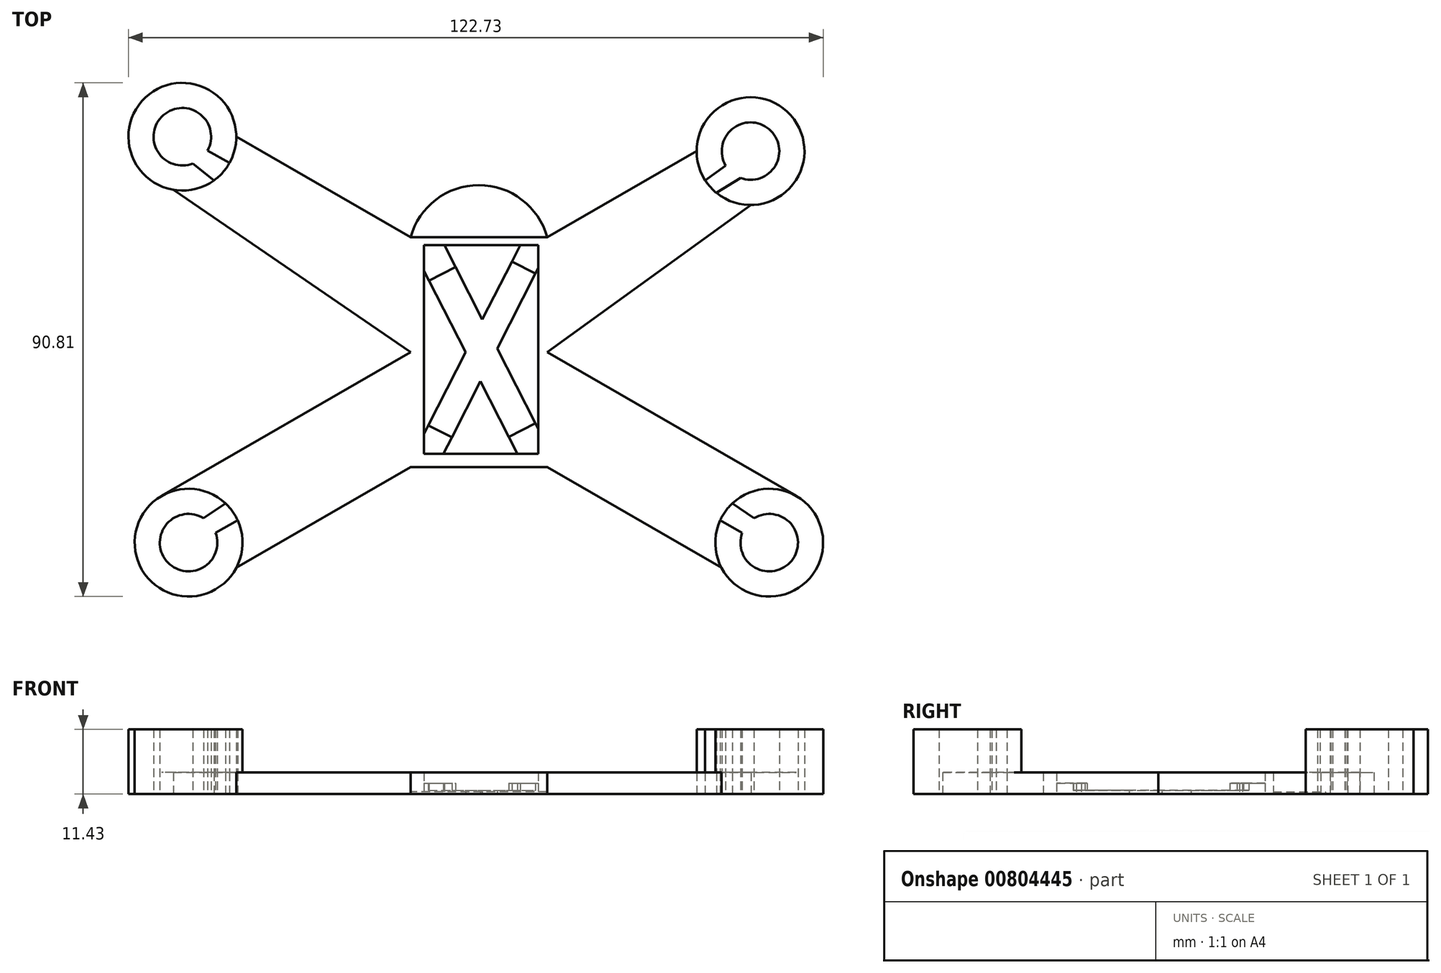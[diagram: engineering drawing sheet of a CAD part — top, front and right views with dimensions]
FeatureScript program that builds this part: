
annotation { "Feature Type Name" : "Feature", "Feature Type Description" : "" }
export const myFeature = defineFeature(function(context is Context, id is Id, definition is map)
    precondition{}
    {
        {
            var Q0;
            Q0=qCreatedBy(makeId("Top.planeOp"),FACE);
            var sketch = newSketch(context, id + "F0", { "sketchPlane" : qUnion([Q0])});
            skLineSegment(sketch, "E0.bottom", {"start": v(0, 0) * mm, "end": v(-24.13, 0) * mm});
            skLineSegment(sketch, "E0.top", {"start": v(0, 40.64) * mm, "end": v(-24.13, 40.64) * mm});
            skLineSegment(sketch, "E0.left", {"start": v(0, 0) * mm, "end": v(0, 40.64) * mm});
            skLineSegment(sketch, "E0.right", {"start": v(-24.13, 0) * mm, "end": v(-24.13, 40.64) * mm});
            skLineSegment(sketch, "E1", {"start": v(0, 40.64) * mm, "end": v(26.4, 55.88) * mm});
            skCircle(sketch, "E2", {"center": v(35.92, 55.88) * mm, "radius": 5.08 * mm});
            skCircle(sketch, "E3", {"center": v(35.92, 55.88) * mm, "radius": 9.53 * mm});
            skLineSegment(sketch, "E4", {"start": v(36.03, 46.36) * mm, "end": v(0, 20.32) * mm});
            skLineSegment(sketch, "E5", {"start": v(0, 0) * mm, "end": v(30.8, -17.78) * mm});
            skLineSegment(sketch, "E6", {"start": v(0, 20.32) * mm, "end": v(43.99, -5.1) * mm});
            skCircle(sketch, "E7", {"center": v(39.22, -13.34) * mm, "radius": 9.53 * mm});
            skCircle(sketch, "E8", {"center": v(39.22, -13.34) * mm, "radius": 5.08 * mm});
            skLineSegment(sketch, "E9.MirrorCS", {"start": v(-66.04, 49.03) * mm, "end": v(-24.13, 20.32) * mm});
            skLineSegment(sketch, "E10.MirrorCS", {"start": v(-24.13, 40.64) * mm, "end": v(-54.93, 58.42) * mm});
            skCircle(sketch, "E11.MirrorC", {"center": v(-64.45, 58.42) * mm, "radius": 9.53 * mm});
            skCircle(sketch, "E12.MirrorC", {"center": v(-64.45, 58.42) * mm, "radius": 5.08 * mm});
            skLineSegment(sketch, "E13.MirrorCS", {"start": v(-24.13, 0) * mm, "end": v(-54.93, -17.78) * mm});
            skLineSegment(sketch, "E14.MirrorCS", {"start": v(-24.13, 20.32) * mm, "end": v(-68.12, -5.1) * mm});
            skCircle(sketch, "E15.MirrorC", {"center": v(-63.35, -13.34) * mm, "radius": 5.08 * mm});
            skCircle(sketch, "E16.MirrorC", {"center": v(-63.35, -13.34) * mm, "radius": 9.53 * mm});
            skLineSegment(sketch, "E17.bottom", {"start": v(-21.78, 2.4) * mm, "end": v(-1.57, 2.4) * mm});
            skLineSegment(sketch, "E17.top", {"start": v(-21.78, 39.23) * mm, "end": v(-1.57, 39.23) * mm});
            skLineSegment(sketch, "E17.left", {"start": v(-21.78, 2.4) * mm, "end": v(-21.78, 39.23) * mm});
            skLineSegment(sketch, "E17.right", {"start": v(-1.57, 2.4) * mm, "end": v(-1.57, 39.23) * mm});
            skLineSegment(sketch, "E18", {"start": v(-21.78, 34.72) * mm, "end": v(-14.42, 20.3) * mm});
            skLineSegment(sketch, "E19", {"start": v(-18.16, 39.23) * mm, "end": v(-11.46, 26.11) * mm});
            skLineSegment(sketch, "E20", {"start": v(-21.78, 5.9) * mm, "end": v(-14.42, 20.3) * mm});
            skLineSegment(sketch, "E21", {"start": v(-18.33, 2.4) * mm, "end": v(-11.8, 15.18) * mm});
            skLineSegment(sketch, "E22.trimOffspring", {"start": v(-8.84, 20.98) * mm, "end": v(-1.57, 35.24) * mm});
            skLineSegment(sketch, "E23.trimOffspring", {"start": v(-11.46, 26.11) * mm, "end": v(-4.76, 39.23) * mm});
            skLineSegment(sketch, "E24.trimOffspring", {"start": v(-8.84, 20.98) * mm, "end": v(-1.57, 6.74) * mm});
            skLineSegment(sketch, "E25.trimOffspring", {"start": v(-11.8, 15.18) * mm, "end": v(-5.27, 2.4) * mm});
            skLineSegment(sketch, "E26", {"start": v(-21, 7.41) * mm, "end": v(-16.85, 5.3) * mm});
            skLineSegment(sketch, "E27", {"start": v(-20.9, 33) * mm, "end": v(-16.2, 35.4) * mm});
            skLineSegment(sketch, "E28", {"start": v(-6.23, 36.36) * mm, "end": v(-2.07, 34.24) * mm});
            skLineSegment(sketch, "E29", {"start": v(-6.79, 5.36) * mm, "end": v(-2.09, 7.76) * mm});
            skArc(sketch, "E30", {"start": v(0, 40.64) * mm, "mid": v(-12.07, 49.86) * mm, "end": v(-24.13, 40.64) * mm});
            skLineSegment(sketch, "E31", {"start": v(34.44, -11.62) * mm, "end": v(30.56, -9.38) * mm});
            skLineSegment(sketch, "E32", {"start": v(36.55, -9.02) * mm, "end": v(32.69, -6.4) * mm});
            skLineSegment(sketch, "E33.MirrorCS", {"start": v(-58.57, -11.62) * mm, "end": v(-54.69, -9.38) * mm});
            skLineSegment(sketch, "E34.MirrorCS", {"start": v(-60.68, -9.02) * mm, "end": v(-56.82, -6.4) * mm});
            skLineSegment(sketch, "E35", {"start": v(-62.58, 53.7) * mm, "end": v(-58.86, 50.7) * mm});
            skLineSegment(sketch, "E36", {"start": v(-60, 55.97) * mm, "end": v(-56.1, 53.82) * mm});
            skLineSegment(sketch, "E37", {"start": v(34.15, 51.12) * mm, "end": v(29.9, 48.5) * mm});
            skLineSegment(sketch, "E38", {"start": v(31.53, 53.33) * mm, "end": v(27.91, 50.72) * mm});
            skSolve(sketch);
        }
        {
            var Q0;
            {var subQ0=sQuery(id+"F0.wireOp",EDGE,"E1");Q0=makeQuery(id+"F0.imprint","IMPRINT",FACE,{"disambiguationData":[TD([[makeQuery(id+"F0.imprint","IMPRINT",EDGE,{"derivedFrom":subQ0}),-1.0]])]});}
            var Q1;
            {var subQ0=sQuery(id+"F0.wireOp",EDGE,"E5");Q1=makeQuery(id+"F0.imprint","IMPRINT",FACE,{"disambiguationData":[TD([[makeQuery(id+"F0.imprint","IMPRINT",EDGE,{"derivedFrom":subQ0}),1.0]])]});}
            var Q2;
            {var subQ0=sQuery(id+"F0.wireOp",EDGE,"E13.MirrorCS");Q2=makeQuery(id+"F0.imprint","IMPRINT",FACE,{"disambiguationData":[TD([[makeQuery(id+"F0.imprint","IMPRINT",EDGE,{"derivedFrom":subQ0}),-1.0]])]});}
            var Q3;
            {var subQ2=sQuery(id+"F0.wireOp",EDGE,"E9.MirrorCS");Q3=makeQuery(id+"F0.imprint","IMPRINT",FACE,{"disambiguationData":[TD([[makeQuery(id+"F0.imprint","IMPRINT",EDGE,{"derivedFrom":subQ2}),1.0]])]});}
            var Q4;
            {var subQ3=sQuery(id+"F0.wireOp",EDGE,"E0.bottom");Q4=makeQuery(id+"F0.imprint","IMPRINT",FACE,{"disambiguationData":[TD([[makeQuery(id+"F0.imprint","IMPRINT",EDGE,{"derivedFrom":subQ3}),-1.0]])]});}
            extrude(context, id + "F1", {"entities" : qUnion([Q0, Q1, Q2, Q3, Q4]), "depth" : 3.8 * mm, "offsetDistance" : 25.4 * mm});
        }
        {
            var Q0;
            {var subQ3=sQuery(id+"F0.wireOp",EDGE,"E31");Q0=makeQuery(id+"F0.imprint","IMPRINT",FACE,{"disambiguationData":[TD([[makeQuery(id+"F0.imprint","IMPRINT",EDGE,{"derivedFrom":subQ3}),1.0]])]});}
            var Q1;
            {var subQ3=sQuery(id+"F0.wireOp",EDGE,"E33.MirrorCS");Q1=makeQuery(id+"F0.imprint","IMPRINT",FACE,{"disambiguationData":[TD([[makeQuery(id+"F0.imprint","IMPRINT",EDGE,{"derivedFrom":subQ3}),-1.0]])]});}
            var Q2;
            {var subQ3=sQuery(id+"F0.wireOp",EDGE,"E35");Q2=makeQuery(id+"F0.imprint","IMPRINT",FACE,{"disambiguationData":[TD([[makeQuery(id+"F0.imprint","IMPRINT",EDGE,{"derivedFrom":subQ3}),-1.0]])]});}
            var Q3;
            {var subQ4=sQuery(id+"F0.wireOp",EDGE,"E37");Q3=makeQuery(id+"F0.imprint","IMPRINT",FACE,{"disambiguationData":[TD([[makeQuery(id+"F0.imprint","IMPRINT",EDGE,{"derivedFrom":subQ4}),1.0]])]});}
            extrude(context, id + "F2", {"entities" : qUnion([Q0, Q1, Q2, Q3]), "operationType" : NewBodyOperationType.ADD, "depth" : 11.43 * mm, "offsetDistance" : 25.4 * mm});
        }
        {
            var Q0;
            {var subQ13=sQuery(id+"F0.wireOp",EDGE,"E24.trimOffspring");Q0=makeQuery(id+"F0.imprint","IMPRINT",FACE,{"disambiguationData":[TD([[makeQuery(id+"F0.imprint","IMPRINT",EDGE,{"derivedFrom":subQ13}),-1.0]])]});}
            var Q1;
            {var subQ3=sQuery(id+"F0.wireOp",EDGE,"E26");Q1=makeQuery(id+"F0.imprint","IMPRINT",FACE,{"disambiguationData":[TD([[makeQuery(id+"F0.imprint","IMPRINT",EDGE,{"derivedFrom":subQ3}),-1.0]])]});}
            var Q2;
            {var subQ3=sQuery(id+"F0.wireOp",EDGE,"E28");Q2=makeQuery(id+"F0.imprint","IMPRINT",FACE,{"disambiguationData":[TD([[makeQuery(id+"F0.imprint","IMPRINT",EDGE,{"derivedFrom":subQ3}),1.0]])]});}
            var Q3;
            {var subQ3=sQuery(id+"F0.wireOp",EDGE,"E27");Q3=makeQuery(id+"F0.imprint","IMPRINT",FACE,{"disambiguationData":[TD([[makeQuery(id+"F0.imprint","IMPRINT",EDGE,{"derivedFrom":subQ3}),1.0]])]});}
            extrude(context, id + "F3", {"entities" : qUnion([Q0, Q1, Q2, Q3]), "operationType" : NewBodyOperationType.ADD, "depth" : 1.9 * mm, "offsetDistance" : 25.4 * mm});
        }
        {
            var Q0;
            {var subQ15=sQuery(id+"F0.wireOp",EDGE,"E26");Q0=makeQuery(id+"F0.imprint","IMPRINT",FACE,{"disambiguationData":[TD([[makeQuery(id+"F0.imprint","IMPRINT",EDGE,{"derivedFrom":subQ15}),1.0]])]});}
            extrude(context, id + "F4", {"entities" : qUnion([Q0]), "operationType" : NewBodyOperationType.ADD, "depth" : 0.64 * mm, "offsetDistance" : 25.4 * mm});
        }
        {
            var Q0;
            Q0=makeQuery(id+"F0.imprint","IMPRINT",FACE,{"disambiguationData":[TD([[makeQuery(id+"F0.imprint","IMPRINT",EDGE,{"derivedFrom":sQuery(id+"F0.wireOp",EDGE,"E0.top")}),-1.0]])]});
            extrude(context, id + "F5", {"entities" : qUnion([Q0]), "operationType" : NewBodyOperationType.ADD, "depth" : 0.38 * mm, "offsetDistance" : 25.4 * mm});
        }
    });
